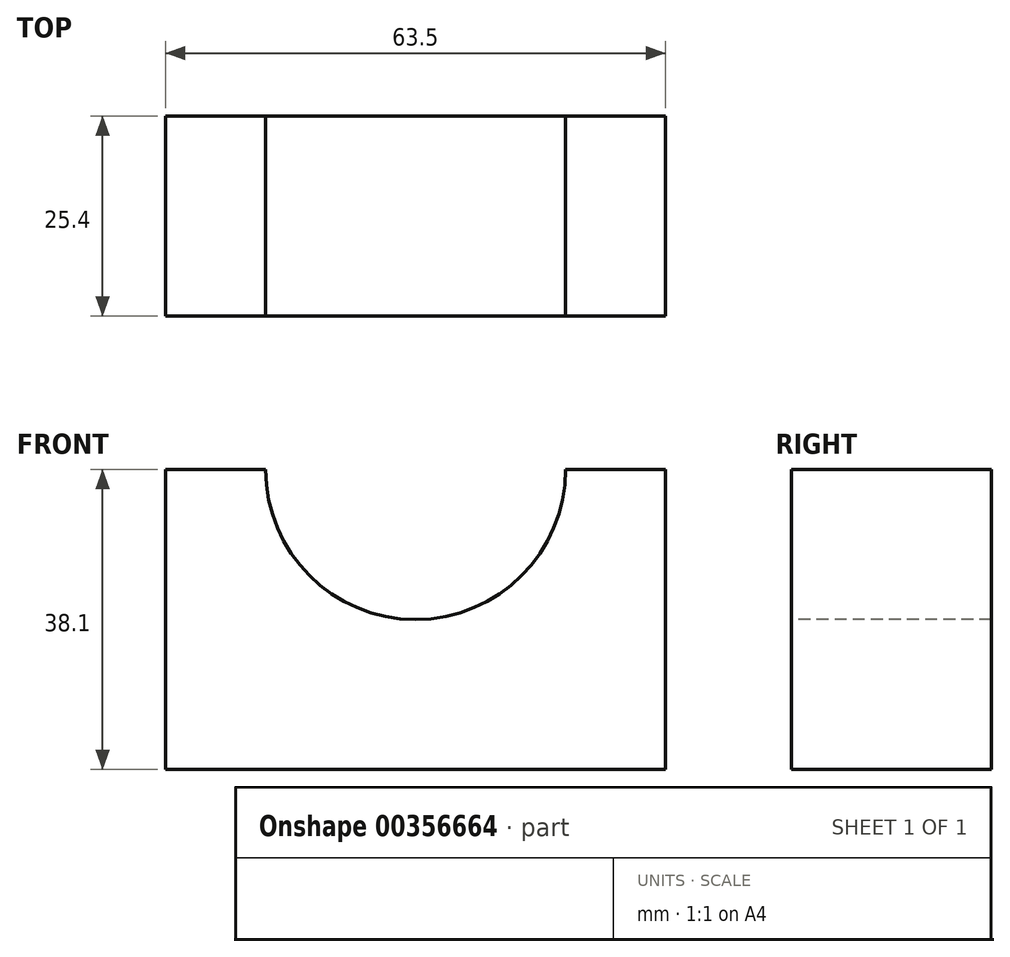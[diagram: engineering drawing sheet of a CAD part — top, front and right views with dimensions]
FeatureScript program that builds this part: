
annotation { "Feature Type Name" : "Feature", "Feature Type Description" : "" }
export const myFeature = defineFeature(function(context is Context, id is Id, definition is map)
    precondition{}
    {
        {
            var Q0;
            Q0=qCreatedBy(makeId("Front.planeOp"),FACE);
            var sketch = newSketch(context, id + "F0", { "sketchPlane" : qUnion([Q0])});
            skLineSegment(sketch, "E0", {"start": v(-43.02, 26.02) * mm, "end": v(20.48, 26.02) * mm});
            skLineSegment(sketch, "E1", {"start": v(20.48, 26.02) * mm, "end": v(20.48, -12.08) * mm});
            skLineSegment(sketch, "E2", {"start": v(20.48, -12.08) * mm, "end": v(-43.02, -12.08) * mm});
            skLineSegment(sketch, "E3", {"start": v(-43.02, -12.08) * mm, "end": v(-43.02, 26.02) * mm});
            skSolve(sketch);
        }
        {
            var Q0;
            Q0=makeQuery(id+"F0.imprint","IMPRINT",FACE,{"disambiguationData":[TD([[makeQuery(id+"F0.imprint","IMPRINT",EDGE,{"derivedFrom":sQuery(id+"F0.wireOp",EDGE,"E0")}),-1.0]])]});
            extrude(context, id + "F1", {"entities" : qUnion([Q0]), "depth" : 25.4 * mm});
        }
        {
            var Q0;
            Q0=makeQuery(id+"F1.opExtrude","CAP_FACE",FACE,{"disambiguationData":[OSD([sQuery(id+"F0.wireOp",EDGE,"E0"),sQuery(id+"F0.wireOp",EDGE,"E1"),sQuery(id+"F0.wireOp",EDGE,"E2"),sQuery(id+"F0.wireOp",EDGE,"E3")])],"isStart":false});
            var sketch = newSketch(context, id + "F2", { "sketchPlane" : qUnion([Q0])});
            skArc(sketch, "E4", {"start": v(-30.32, 26.02) * mm, "mid": v(-11.27, 6.97) * mm, "end": v(7.78, 26.02) * mm});
            skLineSegment(sketch, "E5", {"start": v(7.78, 26.02) * mm, "end": v(20.48, 26.02) * mm});
            skLineSegment(sketch, "E6", {"start": v(7.78, 26.02) * mm, "end": v(-30.32, 26.02) * mm});
            skLineSegment(sketch, "E7", {"start": v(-30.32, 26.02) * mm, "end": v(-43.02, 26.02) * mm});
            skSolve(sketch);
        }
        {
            var Q0;
            Q0=makeQuery(id+"F2.imprint","IMPRINT",FACE,{"disambiguationData":[TD([[makeQuery(id+"F2.imprint","IMPRINT",EDGE,{"derivedFrom":sQuery(id+"F2.wireOp",EDGE,"E4")}),1.0]])]});
            extrude(context, id + "F3", {"entities" : qUnion([Q0]), "operationType" : NewBodyOperationType.REMOVE, "oppositeDirection" : true, "depth" : 25.4 * mm});
        }
    });
